# Revit family: Network Video Endpoint-Q-SYS-NV-1-H-WE-Surface Mounted pu mat 1
name_source: partatom
category: Communication Devices
units: mm (PartAtom-declared; Revit-internal decimal feet)

## family parameters
Cut with Voids When Loaded = No
Host = Face
Maintain Annotation Orientation = No
OmniClass Number = 23.85.10.14
OmniClass Title = Visual Information Systems
Part Type = Normal
Room Calculation Point = No
Round Connector Dimension = Use Diameter
Shared = No

## types (1)
- White
    Body Height = 71 mm  [stored 0.23294 ft]
    Body Material = Plastic - Q-SYS - Black
    Body Width = 87 mm  [stored 0.285433 ft]
    Default Elevation = 1219.2 mm  [stored 4 ft]
    Depth = 67.9 mm  [stored 0.222769 ft]
    Description = Network video endpoint for Q-SYS platform
    Height = 124.7 mm
    Highlight Material = Plastic - Q-SYS - White Mesh
    IQ Category = Network Video Endpoint
    Manufacturer = Q-SYS
    Manufacturer URL = https://www.qsys.com
    Model = NV-1-H-WE
    Plate Material = Plastic - Q-SYS - White
    Product Documentation Link = https://www.qsys.com
    Product Page URL = https://www.qsys.com
    Type Comments = White
    URL = https://www.qsys.com
    Weight = 0.84 lbm
    Weight Dimensional = 0.84
    Weight Product = 0.84
    Width = 124.7 mm

note: [stored X ft] marks values corroborated as IEEE doubles in the binary element streams (Revit-internal decimal feet)

## geometry (parser evidence)
native form markers: Sweep x5
no freeform markers — native parametric forms only
